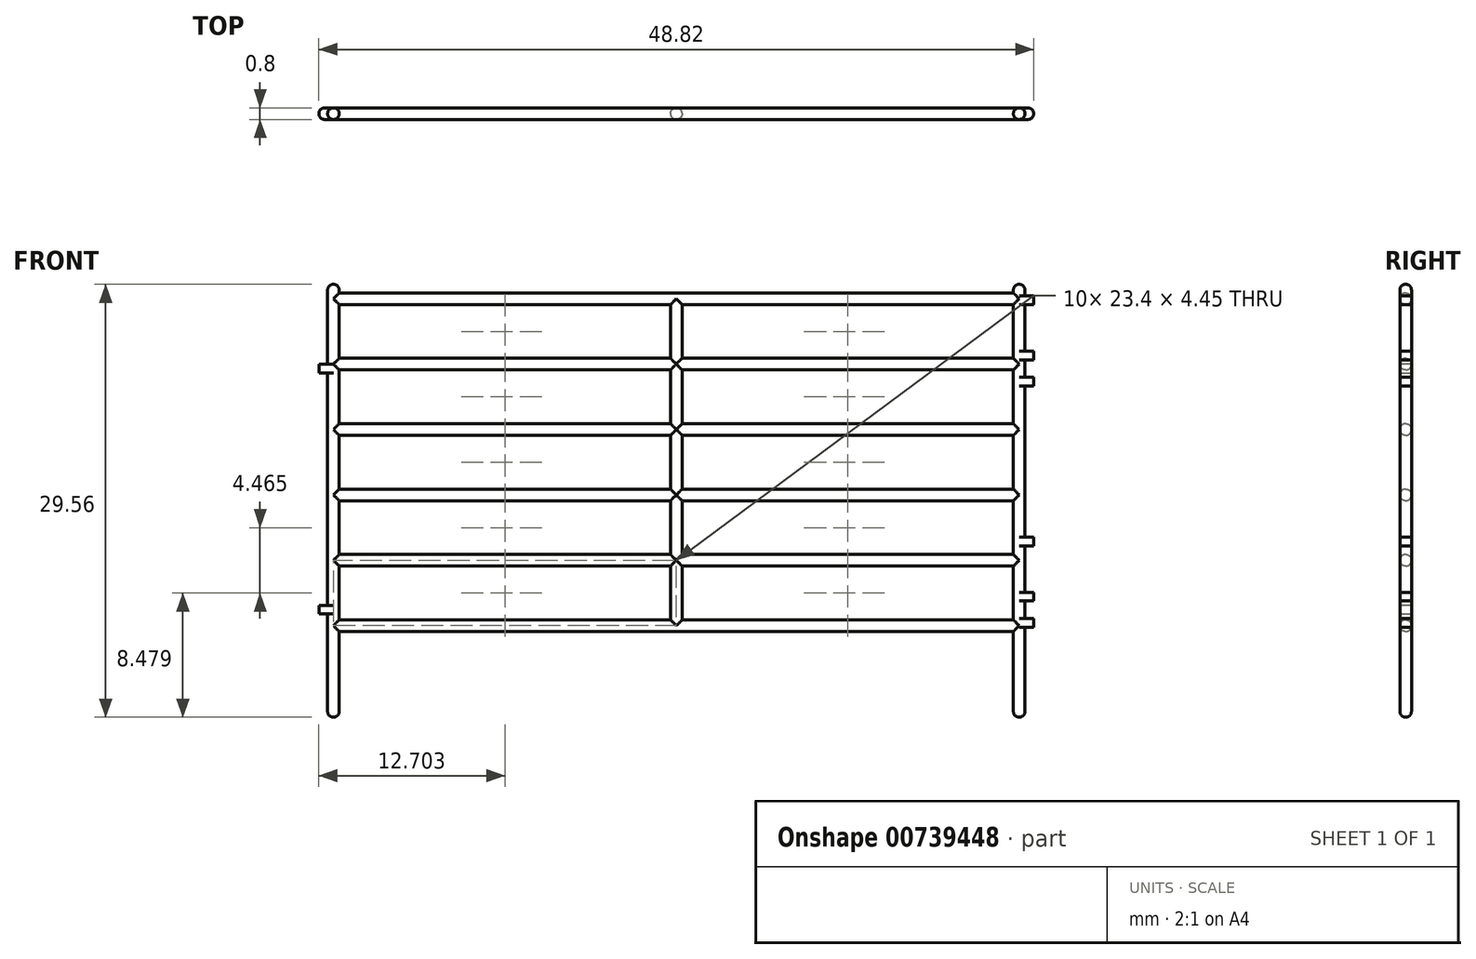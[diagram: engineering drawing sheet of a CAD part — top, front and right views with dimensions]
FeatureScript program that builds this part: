
annotation { "Feature Type Name" : "Feature", "Feature Type Description" : "" }
export const myFeature = defineFeature(function(context is Context, id is Id, definition is map)
    precondition{}
    {
        {
            var Q0;
            Q0=qCreatedBy(makeId("Front.planeOp"),FACE);
            var sketch = newSketch(context, id + "F0", { "sketchPlane" : qUnion([Q0])});
            skLineSegment(sketch, "E0", {"start": v(0, 0) * mm, "end": v(-46.04, 0) * mm});
            skLineSegment(sketch, "E1.0", {"start": v(0, 0.8) * mm, "end": v(-22.62, 0.8) * mm});
            skLineSegment(sketch, "E2.0", {"start": v(0, 4.46) * mm, "end": v(-22.62, 4.46) * mm});
            skLineSegment(sketch, "E3.0", {"start": v(0, 5.26) * mm, "end": v(-22.62, 5.26) * mm});
            skLineSegment(sketch, "E4.0", {"start": v(0, 8.93) * mm, "end": v(-22.62, 8.93) * mm});
            skLineSegment(sketch, "E5.0", {"start": v(0, 9.72) * mm, "end": v(-22.62, 9.72) * mm});
            skLineSegment(sketch, "E6.0", {"start": v(0, 13.4) * mm, "end": v(-22.62, 13.4) * mm});
            skLineSegment(sketch, "E7.0", {"start": v(0, 14.19) * mm, "end": v(-22.62, 14.19) * mm});
            skLineSegment(sketch, "E8.0", {"start": v(0, 17.86) * mm, "end": v(-22.62, 17.86) * mm});
            skLineSegment(sketch, "E9.0", {"start": v(0, 18.65) * mm, "end": v(-22.62, 18.65) * mm});
            skLineSegment(sketch, "E10.0", {"start": v(0, 22.32) * mm, "end": v(-22.62, 22.32) * mm});
            skLineSegment(sketch, "E11.0", {"start": v(0, 23.12) * mm, "end": v(-46.04, 23.12) * mm});
            skLineSegment(sketch, "E12", {"start": v(0, 22.32) * mm, "end": v(0, 18.65) * mm});
            skLineSegment(sketch, "E13.0", {"start": v(0.8, 23.12) * mm, "end": v(0.8, 22.92) * mm});
            skLineSegment(sketch, "E14", {"start": v(-46.04, 22.32) * mm, "end": v(-46.04, 18.65) * mm});
            skLineSegment(sketch, "E15.0", {"start": v(-46.83, 23.12) * mm, "end": v(-46.83, 18.26) * mm});
            skPoint(sketch, "E16", {"position": v(0, 23.32) * mm});
            skLineSegment(sketch, "E17", {"start": v(0, 23.12) * mm, "end": v(0, 23.32) * mm});
            skLineSegment(sketch, "E18", {"start": v(0.8, 23.32) * mm, "end": v(0.8, 23.12) * mm});
            skArc(sketch, "E19", {"start": v(0, 23.32) * mm, "mid": v(0.4, 23.71) * mm, "end": v(0.8, 23.32) * mm});
            skPoint(sketch, "E20", {"position": v(-46.04, 23.32) * mm});
            skLineSegment(sketch, "E21", {"start": v(-46.04, 23.12) * mm, "end": v(-46.04, 23.32) * mm});
            skLineSegment(sketch, "E22", {"start": v(-46.83, 23.32) * mm, "end": v(-46.83, 23.12) * mm});
            skArc(sketch, "E23", {"start": v(-46.83, 23.32) * mm, "mid": v(-46.43, 23.71) * mm, "end": v(-46.04, 23.32) * mm});
            skArc(sketch, "E24", {"start": v(0.8, -5.46) * mm, "mid": v(0.4, -5.85) * mm, "end": v(0, -5.46) * mm});
            skArc(sketch, "E25", {"start": v(-46.04, -5.46) * mm, "mid": v(-46.43, -5.85) * mm, "end": v(-46.83, -5.46) * mm});
            skPoint(sketch, "E26", {"position": v(-23.42, 0.8) * mm});
            skLineSegment(sketch, "E27", {"start": v(-23.42, 0.8) * mm, "end": v(-23.42, 4.46) * mm});
            skLineSegment(sketch, "E28", {"start": v(-23.42, 5.26) * mm, "end": v(-23.42, 8.93) * mm});
            skLineSegment(sketch, "E29", {"start": v(-23.42, 9.72) * mm, "end": v(-23.42, 13.4) * mm});
            skLineSegment(sketch, "E30", {"start": v(-23.42, 14.19) * mm, "end": v(-23.42, 17.86) * mm});
            skPoint(sketch, "E30.endSnap0", {"position": v(-23.02, 17.86) * mm});
            skLineSegment(sketch, "E31", {"start": v(-23.42, 18.65) * mm, "end": v(-23.42, 22.32) * mm});
            skLineSegment(sketch, "E32.0", {"start": v(-22.62, 18.65) * mm, "end": v(-22.62, 22.32) * mm});
            skLineSegment(sketch, "E33.0", {"start": v(-22.62, 14.19) * mm, "end": v(-22.62, 17.86) * mm});
            skLineSegment(sketch, "E34.0", {"start": v(-22.62, 9.72) * mm, "end": v(-22.62, 13.4) * mm});
            skLineSegment(sketch, "E35.0", {"start": v(-22.62, 5.26) * mm, "end": v(-22.62, 8.93) * mm});
            skLineSegment(sketch, "E36.0", {"start": v(-22.62, 0.8) * mm, "end": v(-22.62, 4.46) * mm});
            skLineSegment(sketch, "E37.trimOffspring", {"start": v(-23.42, 0.8) * mm, "end": v(-46.04, 0.8) * mm});
            skLineSegment(sketch, "E38.trimOffspring", {"start": v(-23.42, 4.46) * mm, "end": v(-46.04, 4.46) * mm});
            skLineSegment(sketch, "E39.trimOffspring", {"start": v(-23.42, 5.26) * mm, "end": v(-46.04, 5.26) * mm});
            skLineSegment(sketch, "E40.trimOffspring", {"start": v(-23.42, 8.93) * mm, "end": v(-46.04, 8.93) * mm});
            skLineSegment(sketch, "E41.trimOffspring", {"start": v(-23.42, 9.72) * mm, "end": v(-46.04, 9.72) * mm});
            skLineSegment(sketch, "E42.trimOffspring", {"start": v(-23.42, 13.4) * mm, "end": v(-46.04, 13.4) * mm});
            skLineSegment(sketch, "E43.trimOffspring", {"start": v(-23.42, 14.19) * mm, "end": v(-46.04, 14.19) * mm});
            skLineSegment(sketch, "E44.trimOffspring", {"start": v(-23.42, 17.86) * mm, "end": v(-46.04, 17.86) * mm});
            skLineSegment(sketch, "E45.trimOffspring", {"start": v(-23.42, 18.65) * mm, "end": v(-46.04, 18.65) * mm});
            skLineSegment(sketch, "E46.trimOffspring", {"start": v(-23.42, 22.32) * mm, "end": v(-46.04, 22.32) * mm});
            skLineSegment(sketch, "E47.trimOffspring", {"start": v(-46.04, 17.86) * mm, "end": v(-46.04, 14.19) * mm});
            skLineSegment(sketch, "E48.trimOffspring", {"start": v(-46.04, 13.4) * mm, "end": v(-46.04, 9.72) * mm});
            skLineSegment(sketch, "E49.trimOffspring", {"start": v(-46.04, 8.93) * mm, "end": v(-46.04, 5.26) * mm});
            skLineSegment(sketch, "E50.trimOffspring", {"start": v(-46.04, 4.46) * mm, "end": v(-46.04, 0.8) * mm});
            skLineSegment(sketch, "E51.trimOffspring", {"start": v(-46.04, 0) * mm, "end": v(-46.04, -5.46) * mm});
            skLineSegment(sketch, "E52.trimOffspring", {"start": v(0, 0) * mm, "end": v(0, -5.46) * mm});
            skLineSegment(sketch, "E53.trimOffspring", {"start": v(0, 4.46) * mm, "end": v(0, 0.8) * mm});
            skLineSegment(sketch, "E54.trimOffspring", {"start": v(0, 8.93) * mm, "end": v(0, 5.26) * mm});
            skLineSegment(sketch, "E55.trimOffspring", {"start": v(0, 13.4) * mm, "end": v(0, 9.72) * mm});
            skLineSegment(sketch, "E56.trimOffspring", {"start": v(0, 17.86) * mm, "end": v(0, 14.19) * mm});
            skPoint(sketch, "E57", {"position": v(0.8, 0.3) * mm});
            skLineSegment(sketch, "E58", {"start": v(0.8, 0.3) * mm, "end": v(1.39, 0.3) * mm});
            skLineSegment(sketch, "E59", {"start": v(1.39, 0.3) * mm, "end": v(1.39, 0.9) * mm});
            skLineSegment(sketch, "E60", {"start": v(1.39, 0.9) * mm, "end": v(0.8, 0.9) * mm});
            skPoint(sketch, "E61", {"position": v(0.8, 2.08) * mm});
            skLineSegment(sketch, "E62", {"start": v(0.8, 2.08) * mm, "end": v(1.39, 2.08) * mm});
            skLineSegment(sketch, "E63", {"start": v(1.39, 2.08) * mm, "end": v(1.39, 2.68) * mm});
            skLineSegment(sketch, "E64", {"start": v(1.39, 2.68) * mm, "end": v(0.8, 2.68) * mm});
            skPoint(sketch, "E65", {"position": v(0.8, 5.85) * mm});
            skLineSegment(sketch, "E66", {"start": v(0.8, 5.85) * mm, "end": v(1.39, 5.85) * mm});
            skLineSegment(sketch, "E67", {"start": v(1.39, 5.85) * mm, "end": v(1.39, 6.45) * mm});
            skLineSegment(sketch, "E68", {"start": v(1.39, 6.45) * mm, "end": v(0.8, 6.45) * mm});
            skPoint(sketch, "E69", {"position": v(0.8, 16.77) * mm});
            skLineSegment(sketch, "E70", {"start": v(0.8, 16.77) * mm, "end": v(1.39, 16.77) * mm});
            skLineSegment(sketch, "E71", {"start": v(1.39, 16.77) * mm, "end": v(1.39, 17.36) * mm});
            skLineSegment(sketch, "E72", {"start": v(1.39, 17.36) * mm, "end": v(0.8, 17.36) * mm});
            skPoint(sketch, "E73", {"position": v(0.8, 18.55) * mm});
            skLineSegment(sketch, "E74", {"start": v(0.8, 18.55) * mm, "end": v(1.39, 18.55) * mm});
            skLineSegment(sketch, "E75", {"start": v(1.39, 18.55) * mm, "end": v(1.39, 19.15) * mm});
            skLineSegment(sketch, "E76", {"start": v(1.39, 19.15) * mm, "end": v(0.8, 19.15) * mm});
            skPoint(sketch, "E77", {"position": v(0.8, 22.32) * mm});
            skLineSegment(sketch, "E78", {"start": v(0.8, 22.32) * mm, "end": v(1.39, 22.32) * mm});
            skLineSegment(sketch, "E79", {"start": v(1.39, 22.32) * mm, "end": v(1.39, 22.92) * mm});
            skLineSegment(sketch, "E80", {"start": v(1.39, 22.92) * mm, "end": v(0.8, 22.92) * mm});
            skLineSegment(sketch, "E81.trimOffspring", {"start": v(0.8, 22.32) * mm, "end": v(0.8, 19.15) * mm});
            skLineSegment(sketch, "E82.trimOffspring", {"start": v(0.8, 18.55) * mm, "end": v(0.8, 17.36) * mm});
            skLineSegment(sketch, "E83.trimOffspring", {"start": v(0.8, 16.77) * mm, "end": v(0.8, 6.45) * mm});
            skLineSegment(sketch, "E84.trimOffspring", {"start": v(0.8, 0.3) * mm, "end": v(0.8, -5.46) * mm});
            skLineSegment(sketch, "E85.trimOffspring", {"start": v(0.8, 2.08) * mm, "end": v(0.8, 0.9) * mm});
            skLineSegment(sketch, "E86.trimOffspring", {"start": v(0.8, 5.85) * mm, "end": v(0.8, 2.68) * mm});
            skPoint(sketch, "E87", {"position": v(-46.83, 1.2) * mm});
            skLineSegment(sketch, "E88", {"start": v(-46.83, 1.2) * mm, "end": v(-47.43, 1.2) * mm});
            skLineSegment(sketch, "E89", {"start": v(-47.43, 1.2) * mm, "end": v(-47.43, 1.79) * mm});
            skLineSegment(sketch, "E90", {"start": v(-47.43, 1.79) * mm, "end": v(-46.83, 1.79) * mm});
            skPoint(sketch, "E91", {"position": v(-46.83, 17.66) * mm});
            skLineSegment(sketch, "E92", {"start": v(-46.83, 17.66) * mm, "end": v(-47.43, 17.66) * mm});
            skLineSegment(sketch, "E93", {"start": v(-47.43, 17.66) * mm, "end": v(-47.43, 18.26) * mm});
            skLineSegment(sketch, "E94", {"start": v(-47.43, 18.26) * mm, "end": v(-46.83, 18.26) * mm});
            skLineSegment(sketch, "E95.trimOffspring", {"start": v(-46.83, 17.66) * mm, "end": v(-46.83, 1.79) * mm});
            skLineSegment(sketch, "E96.trimOffspring", {"start": v(-46.83, 1.2) * mm, "end": v(-46.83, -5.46) * mm});
            skSolve(sketch);
        }
        {
            var Q0;
            Q0=makeQuery(id+"F0.imprint","IMPRINT",FACE,{"disambiguationData":[TD([[makeQuery(id+"F0.imprint","IMPRINT",EDGE,{"derivedFrom":sQuery(id+"F0.wireOp",EDGE,"E0")}),-1.0]])]});
            extrude(context, id + "F1", {"entities" : qUnion([Q0]), "endBound" : BoundingType.SYMMETRIC, "depth" : 0.8 * mm, "offsetDistance" : 25.4 * mm});
        }
        {
            var Q0;
            Q0=makeQuery(id+"F1.opExtrude","CAP_EDGE",EDGE,{"disambiguationData":[OSD([sQuery(id+"F0.wireOp",EDGE,"E11.0")])],"isStart":false});
            var Q1;
            Q1=makeQuery(id+"F1.opExtrude","CAP_EDGE",EDGE,{"disambiguationData":[OSD([sQuery(id+"F0.wireOp",EDGE,"E10.0")])],"isStart":false});
            var Q2;
            Q2=makeQuery(id+"F1.opExtrude","CAP_EDGE",EDGE,{"disambiguationData":[OSD([sQuery(id+"F0.wireOp",EDGE,"E17")])],"isStart":false});
            var Q3;
            Q3=makeQuery(id+"F1.opExtrude","CAP_EDGE",EDGE,{"disambiguationData":[OSD([sQuery(id+"F0.wireOp",EDGE,"E19")])],"isStart":false});
            var Q4;
            Q4=makeQuery(id+"F1.opExtrude","CAP_EDGE",EDGE,{"disambiguationData":[OSD([sQuery(id+"F0.wireOp",EDGE,"E79")])],"isStart":false});
            var Q5;
            Q5=makeQuery(id+"F1.opExtrude","CAP_EDGE",EDGE,{"disambiguationData":[OSD([sQuery(id+"F0.wireOp",EDGE,"E13.0"),sQuery(id+"F0.wireOp",EDGE,"E18")])],"isStart":false});
            var Q6;
            Q6=makeQuery(id+"F1.opExtrude","CAP_EDGE",EDGE,{"disambiguationData":[OSD([sQuery(id+"F0.wireOp",EDGE,"E12")])],"isStart":false});
            var Q7;
            Q7=makeQuery(id+"F1.opExtrude","CAP_EDGE",EDGE,{"disambiguationData":[OSD([sQuery(id+"F0.wireOp",EDGE,"E81.trimOffspring")])],"isStart":false});
            var Q8;
            Q8=makeQuery(id+"F1.opExtrude","CAP_EDGE",EDGE,{"disambiguationData":[OSD([sQuery(id+"F0.wireOp",EDGE,"E79")])],"isStart":true});
            var Q9;
            Q9=makeQuery(id+"F1.opExtrude","CAP_EDGE",EDGE,{"disambiguationData":[OSD([sQuery(id+"F0.wireOp",EDGE,"E75")])],"isStart":false});
            var Q10;
            Q10=makeQuery(id+"F1.opExtrude","CAP_EDGE",EDGE,{"disambiguationData":[OSD([sQuery(id+"F0.wireOp",EDGE,"E75")])],"isStart":true});
            var Q11;
            Q11=makeQuery(id+"F1.opExtrude","CAP_EDGE",EDGE,{"disambiguationData":[OSD([sQuery(id+"F0.wireOp",EDGE,"E81.trimOffspring")])],"isStart":true});
            var Q12;
            Q12=makeQuery(id+"F1.opExtrude","CAP_EDGE",EDGE,{"disambiguationData":[OSD([sQuery(id+"F0.wireOp",EDGE,"E13.0"),sQuery(id+"F0.wireOp",EDGE,"E18")])],"isStart":true});
            var Q13;
            Q13=makeQuery(id+"F1.opExtrude","CAP_EDGE",EDGE,{"disambiguationData":[OSD([sQuery(id+"F0.wireOp",EDGE,"E19")])],"isStart":true});
            var Q14;
            Q14=makeQuery(id+"F1.opExtrude","CAP_EDGE",EDGE,{"disambiguationData":[OSD([sQuery(id+"F0.wireOp",EDGE,"E11.0")])],"isStart":true});
            var Q15;
            Q15=makeQuery(id+"F1.opExtrude","CAP_EDGE",EDGE,{"disambiguationData":[OSD([sQuery(id+"F0.wireOp",EDGE,"E9.0")])],"isStart":true});
            var Q16;
            Q16=makeQuery(id+"F1.opExtrude","CAP_EDGE",EDGE,{"disambiguationData":[OSD([sQuery(id+"F0.wireOp",EDGE,"E9.0")])],"isStart":false});
            var Q17;
            Q17=makeQuery(id+"F1.opExtrude","CAP_EDGE",EDGE,{"disambiguationData":[OSD([sQuery(id+"F0.wireOp",EDGE,"E8.0")])],"isStart":false});
            var Q18;
            Q18=makeQuery(id+"F1.opExtrude","CAP_EDGE",EDGE,{"disambiguationData":[OSD([sQuery(id+"F0.wireOp",EDGE,"E82.trimOffspring")])],"isStart":false});
            var Q19;
            Q19=makeQuery(id+"F1.opExtrude","CAP_EDGE",EDGE,{"disambiguationData":[OSD([sQuery(id+"F0.wireOp",EDGE,"E82.trimOffspring")])],"isStart":true});
            var Q20;
            Q20=makeQuery(id+"F1.opExtrude","CAP_EDGE",EDGE,{"disambiguationData":[OSD([sQuery(id+"F0.wireOp",EDGE,"E71")])],"isStart":true});
            var Q21;
            Q21=makeQuery(id+"F1.opExtrude","CAP_EDGE",EDGE,{"disambiguationData":[OSD([sQuery(id+"F0.wireOp",EDGE,"E71")])],"isStart":false});
            var Q22;
            Q22=makeQuery(id+"F1.opExtrude","CAP_EDGE",EDGE,{"disambiguationData":[OSD([sQuery(id+"F0.wireOp",EDGE,"E56.trimOffspring")])],"isStart":false});
            var Q23;
            Q23=makeQuery(id+"F1.opExtrude","CAP_EDGE",EDGE,{"disambiguationData":[OSD([sQuery(id+"F0.wireOp",EDGE,"E83.trimOffspring")])],"isStart":false});
            var Q24;
            Q24=makeQuery(id+"F1.opExtrude","CAP_EDGE",EDGE,{"disambiguationData":[OSD([sQuery(id+"F0.wireOp",EDGE,"E83.trimOffspring")])],"isStart":true});
            var Q25;
            Q25=makeQuery(id+"F1.opExtrude","CAP_EDGE",EDGE,{"disambiguationData":[OSD([sQuery(id+"F0.wireOp",EDGE,"E7.0")])],"isStart":false});
            var Q26;
            Q26=makeQuery(id+"F1.opExtrude","CAP_EDGE",EDGE,{"disambiguationData":[OSD([sQuery(id+"F0.wireOp",EDGE,"E7.0")])],"isStart":true});
            var Q27;
            Q27=makeQuery(id+"F1.opExtrude","CAP_EDGE",EDGE,{"disambiguationData":[OSD([sQuery(id+"F0.wireOp",EDGE,"E6.0")])],"isStart":false});
            var Q28;
            Q28=makeQuery(id+"F1.opExtrude","CAP_EDGE",EDGE,{"disambiguationData":[OSD([sQuery(id+"F0.wireOp",EDGE,"E55.trimOffspring")])],"isStart":false});
            var Q29;
            Q29=makeQuery(id+"F1.opExtrude","CAP_EDGE",EDGE,{"disambiguationData":[OSD([sQuery(id+"F0.wireOp",EDGE,"E5.0")])],"isStart":false});
            var Q30;
            Q30=makeQuery(id+"F1.opExtrude","CAP_EDGE",EDGE,{"disambiguationData":[OSD([sQuery(id+"F0.wireOp",EDGE,"E5.0")])],"isStart":true});
            var Q31;
            Q31=makeQuery(id+"F1.opExtrude","CAP_EDGE",EDGE,{"disambiguationData":[OSD([sQuery(id+"F0.wireOp",EDGE,"E4.0")])],"isStart":false});
            var Q32;
            Q32=makeQuery(id+"F1.opExtrude","CAP_EDGE",EDGE,{"disambiguationData":[OSD([sQuery(id+"F0.wireOp",EDGE,"E54.trimOffspring")])],"isStart":false});
            var Q33;
            Q33=makeQuery(id+"F1.opExtrude","CAP_EDGE",EDGE,{"disambiguationData":[OSD([sQuery(id+"F0.wireOp",EDGE,"E67")])],"isStart":true});
            var Q34;
            Q34=makeQuery(id+"F1.opExtrude","CAP_EDGE",EDGE,{"disambiguationData":[OSD([sQuery(id+"F0.wireOp",EDGE,"E67")])],"isStart":false});
            var Q35;
            Q35=makeQuery(id+"F1.opExtrude","CAP_EDGE",EDGE,{"disambiguationData":[OSD([sQuery(id+"F0.wireOp",EDGE,"E86.trimOffspring")])],"isStart":false});
            var Q36;
            Q36=makeQuery(id+"F1.opExtrude","CAP_EDGE",EDGE,{"disambiguationData":[OSD([sQuery(id+"F0.wireOp",EDGE,"E86.trimOffspring")])],"isStart":true});
            var Q37;
            Q37=makeQuery(id+"F1.opExtrude","CAP_EDGE",EDGE,{"disambiguationData":[OSD([sQuery(id+"F0.wireOp",EDGE,"E3.0")])],"isStart":false});
            var Q38;
            Q38=makeQuery(id+"F1.opExtrude","CAP_EDGE",EDGE,{"disambiguationData":[OSD([sQuery(id+"F0.wireOp",EDGE,"E3.0")])],"isStart":true});
            var Q39;
            Q39=makeQuery(id+"F1.opExtrude","CAP_EDGE",EDGE,{"disambiguationData":[OSD([sQuery(id+"F0.wireOp",EDGE,"E2.0")])],"isStart":false});
            var Q40;
            Q40=makeQuery(id+"F1.opExtrude","CAP_EDGE",EDGE,{"disambiguationData":[OSD([sQuery(id+"F0.wireOp",EDGE,"E53.trimOffspring")])],"isStart":false});
            var Q41;
            Q41=makeQuery(id+"F1.opExtrude","CAP_EDGE",EDGE,{"disambiguationData":[OSD([sQuery(id+"F0.wireOp",EDGE,"E63")])],"isStart":false});
            var Q42;
            Q42=makeQuery(id+"F1.opExtrude","CAP_EDGE",EDGE,{"disambiguationData":[OSD([sQuery(id+"F0.wireOp",EDGE,"E63")])],"isStart":true});
            var Q43;
            Q43=makeQuery(id+"F1.opExtrude","CAP_EDGE",EDGE,{"disambiguationData":[OSD([sQuery(id+"F0.wireOp",EDGE,"E85.trimOffspring")])],"isStart":false});
            var Q44;
            Q44=makeQuery(id+"F1.opExtrude","CAP_EDGE",EDGE,{"disambiguationData":[OSD([sQuery(id+"F0.wireOp",EDGE,"E85.trimOffspring")])],"isStart":true});
            var Q45;
            Q45=makeQuery(id+"F1.opExtrude","CAP_EDGE",EDGE,{"disambiguationData":[OSD([sQuery(id+"F0.wireOp",EDGE,"E1.0")])],"isStart":false});
            var Q46;
            Q46=makeQuery(id+"F1.opExtrude","CAP_EDGE",EDGE,{"disambiguationData":[OSD([sQuery(id+"F0.wireOp",EDGE,"E1.0")])],"isStart":true});
            var Q47;
            Q47=makeQuery(id+"F1.opExtrude","CAP_EDGE",EDGE,{"disambiguationData":[OSD([sQuery(id+"F0.wireOp",EDGE,"E0")])],"isStart":false});
            var Q48;
            Q48=makeQuery(id+"F1.opExtrude","CAP_EDGE",EDGE,{"disambiguationData":[OSD([sQuery(id+"F0.wireOp",EDGE,"E59")])],"isStart":false});
            var Q49;
            Q49=makeQuery(id+"F1.opExtrude","CAP_EDGE",EDGE,{"disambiguationData":[OSD([sQuery(id+"F0.wireOp",EDGE,"E59")])],"isStart":true});
            var Q50;
            Q50=makeQuery(id+"F1.opExtrude","CAP_EDGE",EDGE,{"disambiguationData":[OSD([sQuery(id+"F0.wireOp",EDGE,"E84.trimOffspring")])],"isStart":false});
            var Q51;
            Q51=makeQuery(id+"F1.opExtrude","CAP_EDGE",EDGE,{"disambiguationData":[OSD([sQuery(id+"F0.wireOp",EDGE,"E84.trimOffspring")])],"isStart":true});
            var Q52;
            Q52=makeQuery(id+"F1.opExtrude","CAP_EDGE",EDGE,{"disambiguationData":[OSD([sQuery(id+"F0.wireOp",EDGE,"E24")])],"isStart":false});
            var Q53;
            Q53=makeQuery(id+"F1.opExtrude","CAP_EDGE",EDGE,{"disambiguationData":[OSD([sQuery(id+"F0.wireOp",EDGE,"E52.trimOffspring")])],"isStart":false});
            var Q54;
            Q54=makeQuery(id+"F1.opExtrude","SWEPT_EDGE",EDGE,{"disambiguationData":[OSD([sQuery(id+"F0.wireOp",EDGE,"E24"),sQuery(id+"F0.wireOp",EDGE,"E84.trimOffspring")])]});
            var Q55;
            Q55=makeQuery(id+"F1.opExtrude","CAP_EDGE",EDGE,{"disambiguationData":[OSD([sQuery(id+"F0.wireOp",EDGE,"E24")])],"isStart":true});
            var Q56;
            Q56=makeQuery(id+"F1.opExtrude","CAP_EDGE",EDGE,{"disambiguationData":[OSD([sQuery(id+"F0.wireOp",EDGE,"E37.trimOffspring")])],"isStart":false});
            var Q57;
            Q57=makeQuery(id+"F1.opExtrude","CAP_EDGE",EDGE,{"disambiguationData":[OSD([sQuery(id+"F0.wireOp",EDGE,"E37.trimOffspring")])],"isStart":true});
            var Q58;
            Q58=makeQuery(id+"F1.opExtrude","CAP_EDGE",EDGE,{"disambiguationData":[OSD([sQuery(id+"F0.wireOp",EDGE,"E27")])],"isStart":false});
            var Q59;
            Q59=makeQuery(id+"F1.opExtrude","CAP_EDGE",EDGE,{"disambiguationData":[OSD([sQuery(id+"F0.wireOp",EDGE,"E36.0")])],"isStart":false});
            var Q60;
            Q60=makeQuery(id+"F1.opExtrude","CAP_EDGE",EDGE,{"disambiguationData":[OSD([sQuery(id+"F0.wireOp",EDGE,"E36.0")])],"isStart":true});
            var Q61;
            Q61=makeQuery(id+"F1.opExtrude","CAP_EDGE",EDGE,{"disambiguationData":[OSD([sQuery(id+"F0.wireOp",EDGE,"E38.trimOffspring")])],"isStart":false});
            var Q62;
            Q62=makeQuery(id+"F1.opExtrude","CAP_EDGE",EDGE,{"disambiguationData":[OSD([sQuery(id+"F0.wireOp",EDGE,"E39.trimOffspring")])],"isStart":false});
            var Q63;
            Q63=makeQuery(id+"F1.opExtrude","CAP_EDGE",EDGE,{"disambiguationData":[OSD([sQuery(id+"F0.wireOp",EDGE,"E39.trimOffspring")])],"isStart":true});
            var Q64;
            Q64=makeQuery(id+"F1.opExtrude","CAP_EDGE",EDGE,{"disambiguationData":[OSD([sQuery(id+"F0.wireOp",EDGE,"E28")])],"isStart":false});
            var Q65;
            Q65=makeQuery(id+"F1.opExtrude","CAP_EDGE",EDGE,{"disambiguationData":[OSD([sQuery(id+"F0.wireOp",EDGE,"E35.0")])],"isStart":false});
            var Q66;
            Q66=makeQuery(id+"F1.opExtrude","CAP_EDGE",EDGE,{"disambiguationData":[OSD([sQuery(id+"F0.wireOp",EDGE,"E35.0")])],"isStart":true});
            var Q67;
            Q67=makeQuery(id+"F1.opExtrude","CAP_EDGE",EDGE,{"disambiguationData":[OSD([sQuery(id+"F0.wireOp",EDGE,"E40.trimOffspring")])],"isStart":false});
            var Q68;
            Q68=makeQuery(id+"F1.opExtrude","CAP_EDGE",EDGE,{"disambiguationData":[OSD([sQuery(id+"F0.wireOp",EDGE,"E41.trimOffspring")])],"isStart":false});
            var Q69;
            Q69=makeQuery(id+"F1.opExtrude","CAP_EDGE",EDGE,{"disambiguationData":[OSD([sQuery(id+"F0.wireOp",EDGE,"E41.trimOffspring")])],"isStart":true});
            var Q70;
            Q70=makeQuery(id+"F1.opExtrude","CAP_EDGE",EDGE,{"disambiguationData":[OSD([sQuery(id+"F0.wireOp",EDGE,"E29")])],"isStart":false});
            var Q71;
            Q71=makeQuery(id+"F1.opExtrude","CAP_EDGE",EDGE,{"disambiguationData":[OSD([sQuery(id+"F0.wireOp",EDGE,"E34.0")])],"isStart":false});
            var Q72;
            Q72=makeQuery(id+"F1.opExtrude","CAP_EDGE",EDGE,{"disambiguationData":[OSD([sQuery(id+"F0.wireOp",EDGE,"E34.0")])],"isStart":true});
            var Q73;
            Q73=makeQuery(id+"F1.opExtrude","CAP_EDGE",EDGE,{"disambiguationData":[OSD([sQuery(id+"F0.wireOp",EDGE,"E42.trimOffspring")])],"isStart":false});
            var Q74;
            Q74=makeQuery(id+"F1.opExtrude","CAP_EDGE",EDGE,{"disambiguationData":[OSD([sQuery(id+"F0.wireOp",EDGE,"E43.trimOffspring")])],"isStart":false});
            var Q75;
            Q75=makeQuery(id+"F1.opExtrude","CAP_EDGE",EDGE,{"disambiguationData":[OSD([sQuery(id+"F0.wireOp",EDGE,"E43.trimOffspring")])],"isStart":true});
            var Q76;
            Q76=makeQuery(id+"F1.opExtrude","CAP_EDGE",EDGE,{"disambiguationData":[OSD([sQuery(id+"F0.wireOp",EDGE,"E30")])],"isStart":false});
            var Q77;
            Q77=makeQuery(id+"F1.opExtrude","CAP_EDGE",EDGE,{"disambiguationData":[OSD([sQuery(id+"F0.wireOp",EDGE,"E33.0")])],"isStart":false});
            var Q78;
            Q78=makeQuery(id+"F1.opExtrude","CAP_EDGE",EDGE,{"disambiguationData":[OSD([sQuery(id+"F0.wireOp",EDGE,"E33.0")])],"isStart":true});
            var Q79;
            Q79=makeQuery(id+"F1.opExtrude","CAP_EDGE",EDGE,{"disambiguationData":[OSD([sQuery(id+"F0.wireOp",EDGE,"E44.trimOffspring")])],"isStart":false});
            var Q80;
            Q80=makeQuery(id+"F1.opExtrude","CAP_EDGE",EDGE,{"disambiguationData":[OSD([sQuery(id+"F0.wireOp",EDGE,"E45.trimOffspring")])],"isStart":false});
            var Q81;
            Q81=makeQuery(id+"F1.opExtrude","CAP_EDGE",EDGE,{"disambiguationData":[OSD([sQuery(id+"F0.wireOp",EDGE,"E45.trimOffspring")])],"isStart":true});
            var Q82;
            Q82=makeQuery(id+"F1.opExtrude","CAP_EDGE",EDGE,{"disambiguationData":[OSD([sQuery(id+"F0.wireOp",EDGE,"E31")])],"isStart":false});
            var Q83;
            Q83=makeQuery(id+"F1.opExtrude","CAP_EDGE",EDGE,{"disambiguationData":[OSD([sQuery(id+"F0.wireOp",EDGE,"E32.0")])],"isStart":false});
            var Q84;
            Q84=makeQuery(id+"F1.opExtrude","CAP_EDGE",EDGE,{"disambiguationData":[OSD([sQuery(id+"F0.wireOp",EDGE,"E32.0")])],"isStart":true});
            var Q85;
            Q85=makeQuery(id+"F1.opExtrude","CAP_EDGE",EDGE,{"disambiguationData":[OSD([sQuery(id+"F0.wireOp",EDGE,"E46.trimOffspring")])],"isStart":false});
            var Q86;
            Q86=makeQuery(id+"F1.opExtrude","CAP_EDGE",EDGE,{"disambiguationData":[OSD([sQuery(id+"F0.wireOp",EDGE,"E14")])],"isStart":false});
            var Q87;
            Q87=makeQuery(id+"F1.opExtrude","CAP_EDGE",EDGE,{"disambiguationData":[OSD([sQuery(id+"F0.wireOp",EDGE,"E14")])],"isStart":true});
            var Q88;
            Q88=makeQuery(id+"F1.opExtrude","CAP_EDGE",EDGE,{"disambiguationData":[OSD([sQuery(id+"F0.wireOp",EDGE,"E21")])],"isStart":false});
            var Q89;
            Q89=makeQuery(id+"F1.opExtrude","CAP_EDGE",EDGE,{"disambiguationData":[OSD([sQuery(id+"F0.wireOp",EDGE,"E21")])],"isStart":true});
            var Q90;
            Q90=makeQuery(id+"F1.opExtrude","CAP_EDGE",EDGE,{"disambiguationData":[OSD([sQuery(id+"F0.wireOp",EDGE,"E23")])],"isStart":true});
            var Q91;
            Q91=makeQuery(id+"F1.opExtrude","CAP_EDGE",EDGE,{"disambiguationData":[OSD([sQuery(id+"F0.wireOp",EDGE,"E23")])],"isStart":false});
            var Q92;
            Q92=makeQuery(id+"F1.opExtrude","CAP_EDGE",EDGE,{"disambiguationData":[OSD([sQuery(id+"F0.wireOp",EDGE,"E15.0"),sQuery(id+"F0.wireOp",EDGE,"E22")])],"isStart":false});
            var Q93;
            Q93=makeQuery(id+"F1.opExtrude","CAP_EDGE",EDGE,{"disambiguationData":[OSD([sQuery(id+"F0.wireOp",EDGE,"E93")])],"isStart":false});
            var Q94;
            Q94=makeQuery(id+"F1.opExtrude","CAP_EDGE",EDGE,{"disambiguationData":[OSD([sQuery(id+"F0.wireOp",EDGE,"E95.trimOffspring")])],"isStart":false});
            var Q95;
            Q95=makeQuery(id+"F1.opExtrude","CAP_EDGE",EDGE,{"disambiguationData":[OSD([sQuery(id+"F0.wireOp",EDGE,"E47.trimOffspring")])],"isStart":false});
            var Q96;
            Q96=makeQuery(id+"F1.opExtrude","CAP_EDGE",EDGE,{"disambiguationData":[OSD([sQuery(id+"F0.wireOp",EDGE,"E47.trimOffspring")])],"isStart":true});
            var Q97;
            Q97=makeQuery(id+"F1.opExtrude","CAP_EDGE",EDGE,{"disambiguationData":[OSD([sQuery(id+"F0.wireOp",EDGE,"E48.trimOffspring")])],"isStart":true});
            var Q98;
            Q98=makeQuery(id+"F1.opExtrude","CAP_EDGE",EDGE,{"disambiguationData":[OSD([sQuery(id+"F0.wireOp",EDGE,"E48.trimOffspring")])],"isStart":false});
            var Q99;
            Q99=makeQuery(id+"F1.opExtrude","CAP_EDGE",EDGE,{"disambiguationData":[OSD([sQuery(id+"F0.wireOp",EDGE,"E49.trimOffspring")])],"isStart":false});
            var Q100;
            Q100=makeQuery(id+"F1.opExtrude","CAP_EDGE",EDGE,{"disambiguationData":[OSD([sQuery(id+"F0.wireOp",EDGE,"E49.trimOffspring")])],"isStart":true});
            var Q101;
            Q101=makeQuery(id+"F1.opExtrude","CAP_EDGE",EDGE,{"disambiguationData":[OSD([sQuery(id+"F0.wireOp",EDGE,"E50.trimOffspring")])],"isStart":false});
            var Q102;
            Q102=makeQuery(id+"F1.opExtrude","CAP_EDGE",EDGE,{"disambiguationData":[OSD([sQuery(id+"F0.wireOp",EDGE,"E50.trimOffspring")])],"isStart":true});
            var Q103;
            Q103=makeQuery(id+"F1.opExtrude","CAP_EDGE",EDGE,{"disambiguationData":[OSD([sQuery(id+"F0.wireOp",EDGE,"E51.trimOffspring")])],"isStart":false});
            var Q104;
            Q104=makeQuery(id+"F1.opExtrude","CAP_EDGE",EDGE,{"disambiguationData":[OSD([sQuery(id+"F0.wireOp",EDGE,"E51.trimOffspring")])],"isStart":true});
            var Q105;
            Q105=makeQuery(id+"F1.opExtrude","CAP_EDGE",EDGE,{"disambiguationData":[OSD([sQuery(id+"F0.wireOp",EDGE,"E96.trimOffspring")])],"isStart":false});
            var Q106;
            Q106=makeQuery(id+"F1.opExtrude","CAP_EDGE",EDGE,{"disambiguationData":[OSD([sQuery(id+"F0.wireOp",EDGE,"E25")])],"isStart":false});
            var Q107;
            Q107=makeQuery(id+"F1.opExtrude","CAP_EDGE",EDGE,{"disambiguationData":[OSD([sQuery(id+"F0.wireOp",EDGE,"E25")])],"isStart":true});
            var Q108;
            Q108=makeQuery(id+"F1.opExtrude","CAP_EDGE",EDGE,{"disambiguationData":[OSD([sQuery(id+"F0.wireOp",EDGE,"E89")])],"isStart":false});
            var Q109;
            Q109=makeQuery(id+"F1.opExtrude","CAP_EDGE",EDGE,{"disambiguationData":[OSD([sQuery(id+"F0.wireOp",EDGE,"E0")])],"isStart":true});
            var Q110;
            Q110=makeQuery(id+"F1.opExtrude","CAP_EDGE",EDGE,{"disambiguationData":[OSD([sQuery(id+"F0.wireOp",EDGE,"E38.trimOffspring")])],"isStart":true});
            var Q111;
            Q111=makeQuery(id+"F1.opExtrude","CAP_EDGE",EDGE,{"disambiguationData":[OSD([sQuery(id+"F0.wireOp",EDGE,"E95.trimOffspring")])],"isStart":true});
            var Q112;
            Q112=makeQuery(id+"F1.opExtrude","CAP_EDGE",EDGE,{"disambiguationData":[OSD([sQuery(id+"F0.wireOp",EDGE,"E89")])],"isStart":true});
            var Q113;
            Q113=makeQuery(id+"F1.opExtrude","CAP_EDGE",EDGE,{"disambiguationData":[OSD([sQuery(id+"F0.wireOp",EDGE,"E96.trimOffspring")])],"isStart":true});
            var Q114;
            Q114=makeQuery(id+"F1.opExtrude","SWEPT_EDGE",EDGE,{"disambiguationData":[OSD([sQuery(id+"F0.wireOp",EDGE,"E25"),sQuery(id+"F0.wireOp",EDGE,"E96.trimOffspring")])]});
            var Q115;
            Q115=makeQuery(id+"F1.opExtrude","CAP_EDGE",EDGE,{"disambiguationData":[OSD([sQuery(id+"F0.wireOp",EDGE,"E40.trimOffspring")])],"isStart":true});
            var Q116;
            Q116=makeQuery(id+"F1.opExtrude","CAP_EDGE",EDGE,{"disambiguationData":[OSD([sQuery(id+"F0.wireOp",EDGE,"E42.trimOffspring")])],"isStart":true});
            var Q117;
            Q117=makeQuery(id+"F1.opExtrude","CAP_EDGE",EDGE,{"disambiguationData":[OSD([sQuery(id+"F0.wireOp",EDGE,"E93")])],"isStart":true});
            var Q118;
            Q118=makeQuery(id+"F1.opExtrude","CAP_EDGE",EDGE,{"disambiguationData":[OSD([sQuery(id+"F0.wireOp",EDGE,"E44.trimOffspring")])],"isStart":true});
            var Q119;
            Q119=makeQuery(id+"F1.opExtrude","CAP_EDGE",EDGE,{"disambiguationData":[OSD([sQuery(id+"F0.wireOp",EDGE,"E46.trimOffspring")])],"isStart":true});
            var Q120;
            Q120=makeQuery(id+"F1.opExtrude","SWEPT_EDGE",EDGE,{"disambiguationData":[OSD([sQuery(id+"F0.wireOp",EDGE,"E22"),sQuery(id+"F0.wireOp",EDGE,"E23")])]});
            var Q121;
            Q121=makeQuery(id+"F1.opExtrude","CAP_EDGE",EDGE,{"disambiguationData":[OSD([sQuery(id+"F0.wireOp",EDGE,"E2.0")])],"isStart":true});
            var Q122;
            Q122=makeQuery(id+"F1.opExtrude","CAP_EDGE",EDGE,{"disambiguationData":[OSD([sQuery(id+"F0.wireOp",EDGE,"E27")])],"isStart":true});
            var Q123;
            Q123=makeQuery(id+"F1.opExtrude","CAP_EDGE",EDGE,{"disambiguationData":[OSD([sQuery(id+"F0.wireOp",EDGE,"E28")])],"isStart":true});
            var Q124;
            Q124=makeQuery(id+"F1.opExtrude","CAP_EDGE",EDGE,{"disambiguationData":[OSD([sQuery(id+"F0.wireOp",EDGE,"E29")])],"isStart":true});
            var Q125;
            Q125=makeQuery(id+"F1.opExtrude","CAP_EDGE",EDGE,{"disambiguationData":[OSD([sQuery(id+"F0.wireOp",EDGE,"E4.0")])],"isStart":true});
            var Q126;
            Q126=makeQuery(id+"F1.opExtrude","CAP_EDGE",EDGE,{"disambiguationData":[OSD([sQuery(id+"F0.wireOp",EDGE,"E6.0")])],"isStart":true});
            var Q127;
            Q127=makeQuery(id+"F1.opExtrude","CAP_EDGE",EDGE,{"disambiguationData":[OSD([sQuery(id+"F0.wireOp",EDGE,"E30")])],"isStart":true});
            var Q128;
            Q128=makeQuery(id+"F1.opExtrude","CAP_EDGE",EDGE,{"disambiguationData":[OSD([sQuery(id+"F0.wireOp",EDGE,"E8.0")])],"isStart":true});
            var Q129;
            Q129=makeQuery(id+"F1.opExtrude","CAP_EDGE",EDGE,{"disambiguationData":[OSD([sQuery(id+"F0.wireOp",EDGE,"E10.0")])],"isStart":true});
            var Q130;
            Q130=makeQuery(id+"F1.opExtrude","CAP_EDGE",EDGE,{"disambiguationData":[OSD([sQuery(id+"F0.wireOp",EDGE,"E31")])],"isStart":true});
            var Q131;
            Q131=makeQuery(id+"F1.opExtrude","CAP_EDGE",EDGE,{"disambiguationData":[OSD([sQuery(id+"F0.wireOp",EDGE,"E12")])],"isStart":true});
            var Q132;
            Q132=makeQuery(id+"F1.opExtrude","CAP_EDGE",EDGE,{"disambiguationData":[OSD([sQuery(id+"F0.wireOp",EDGE,"E56.trimOffspring")])],"isStart":true});
            var Q133;
            Q133=makeQuery(id+"F1.opExtrude","CAP_EDGE",EDGE,{"disambiguationData":[OSD([sQuery(id+"F0.wireOp",EDGE,"E17")])],"isStart":true});
            var Q134;
            Q134=makeQuery(id+"F1.opExtrude","CAP_EDGE",EDGE,{"disambiguationData":[OSD([sQuery(id+"F0.wireOp",EDGE,"E55.trimOffspring")])],"isStart":true});
            var Q135;
            Q135=makeQuery(id+"F1.opExtrude","CAP_EDGE",EDGE,{"disambiguationData":[OSD([sQuery(id+"F0.wireOp",EDGE,"E54.trimOffspring")])],"isStart":true});
            var Q136;
            Q136=makeQuery(id+"F1.opExtrude","CAP_EDGE",EDGE,{"disambiguationData":[OSD([sQuery(id+"F0.wireOp",EDGE,"E53.trimOffspring")])],"isStart":true});
            var Q137;
            Q137=makeQuery(id+"F1.opExtrude","CAP_EDGE",EDGE,{"disambiguationData":[OSD([sQuery(id+"F0.wireOp",EDGE,"E52.trimOffspring")])],"isStart":true});
            var Q138;
            Q138=makeQuery(id+"F1.opExtrude","SWEPT_EDGE",EDGE,{"disambiguationData":[OSD([sQuery(id+"F0.wireOp",EDGE,"E24"),sQuery(id+"F0.wireOp",EDGE,"E52.trimOffspring")])]});
            fillet(context, id + "F2", {"entities" : qUnion([Q0, Q1, Q2, Q3, Q4, Q5, Q6, Q7, Q8, Q9, Q10, Q11, Q12, Q13, Q14, Q15, Q16, Q17, Q18, Q19, Q20, Q21, Q22, Q23, Q24, Q25, Q26, Q27, Q28, Q29, Q30, Q31, Q32, Q33, Q34, Q35, Q36, Q37, Q38, Q39, Q40, Q41, Q42, Q43, Q44, Q45, Q46, Q47, Q48, Q49, Q50, Q51, Q52, Q53, Q54, Q55, Q56, Q57, Q58, Q59, Q60, Q61, Q62, Q63, Q64, Q65, Q66, Q67, Q68, Q69, Q70, Q71, Q72, Q73, Q74, Q75, Q76, Q77, Q78, Q79, Q80, Q81, Q82, Q83, Q84, Q85, Q86, Q87, Q88, Q89, Q90, Q91, Q92, Q93, Q94, Q95, Q96, Q97, Q98, Q99, Q100, Q101, Q102, Q103, Q104, Q105, Q106, Q107, Q108, Q109, Q110, Q111, Q112, Q113, Q114, Q115, Q116, Q117, Q118, Q119, Q120, Q121, Q122, Q123, Q124, Q125, Q126, Q127, Q128, Q129, Q130, Q131, Q132, Q133, Q134, Q135, Q136, Q137, Q138]), "radius" : 0.4 * mm, "tangentPropagation" : true, "allowEdgeOverflow" : false});
        }
    });
